# Revit family: Vitra-Sento-Upper Cabinet-61523-61524-61525
name_source: partatom
category: Furniture Systems
units: mm (PartAtom-declared; Revit-internal decimal feet)

## family parameters
Cut with Voids When Loaded = No
Host = Face
OmniClass Number = 23.40.00.00
OmniClass Title = Equipment and Furnishings
Part Type = Normal
Room Calculation Point = No
Round Connector Dimension = Use Diameter
Shared = Yes

## types (3) — shared parameters
BIMobject category = Storage
Construction Type = Wall Mounted
Default Elevation = 1200 mm
Depth = 355 mm
Description = Sento Upper Cabinet, 70 cm
Design country = Turkey
Height = 700 mm  [stored 2.29659 ft]
IFC Classification = Furniture
Manufacturer = Vitra
Manufacturer name = Vitra
Masterformat 2014 Code = 12 35 30.23
Masterformat 2014 Description = Bathroom Casework
NBS Reference Code = 35-75-08
NBS Reference Description = Bathroom Cabinets
OmniClass Code = 23-31 25 13
OmniClass Description = Bathroom Cabinets
Product certification = https://vitraglobal.com
Product data url = https://www.vitraglobal.com
Product family = Sento
Product group = Bathroom Furniture
Secondary Material = Vitra-Light Oak
Technical description = https://www.vitraglobal.com
UNSPSC Code = 30161801
UNSPSC Description = Bathroom Cabinets
URL = https://vitraglobal.com
Uniclass 1.4 Code = L8241
Uniclass 1.4 Description = Bathroom Cabinets
Uniclass 2.0 Code = PR-35-75-08
Uniclass 2.0 Description = Bathroom Cabinets
Uniclass 2015 Code = Pr_40_30_78_03
Uniclass 2015 Name = Bathroom Cabinets
Uniformat II Code = E2010
Uniformat II Description = Fixed Furnishings
Warranty Period (Year) = 2
Weight Net (kg) = 43,700
Width = 720 mm  [stored 2.3622 ft]
Youtube = https://www.youtube.com
zero-valued in all types: Nominal height, Nominal width

## per-type parameters (varying)
| type | Model | Primary Material | Product SKU |
| Vitra_Sento Upper Cabinet, 70 cm, Matte White_61523 | 61523 | Vitra-MattWhite | 61523 |
| Vitra_Sento Upper Cabinet, 70 cm, Matte Cream_61524 | 61524 | Vitra-Metal | 61524 |
| Vitra_Sento Upper Cabinet, 70 cm, Matte Anthracite_61525 | 61525 | Vitra-DarkOlive | 61525 |

note: [stored X ft] marks values corroborated as IEEE doubles in the binary element streams (Revit-internal decimal feet)

## geometry (parser evidence)
native form markers: Sweep x3
no freeform markers — native parametric forms only
